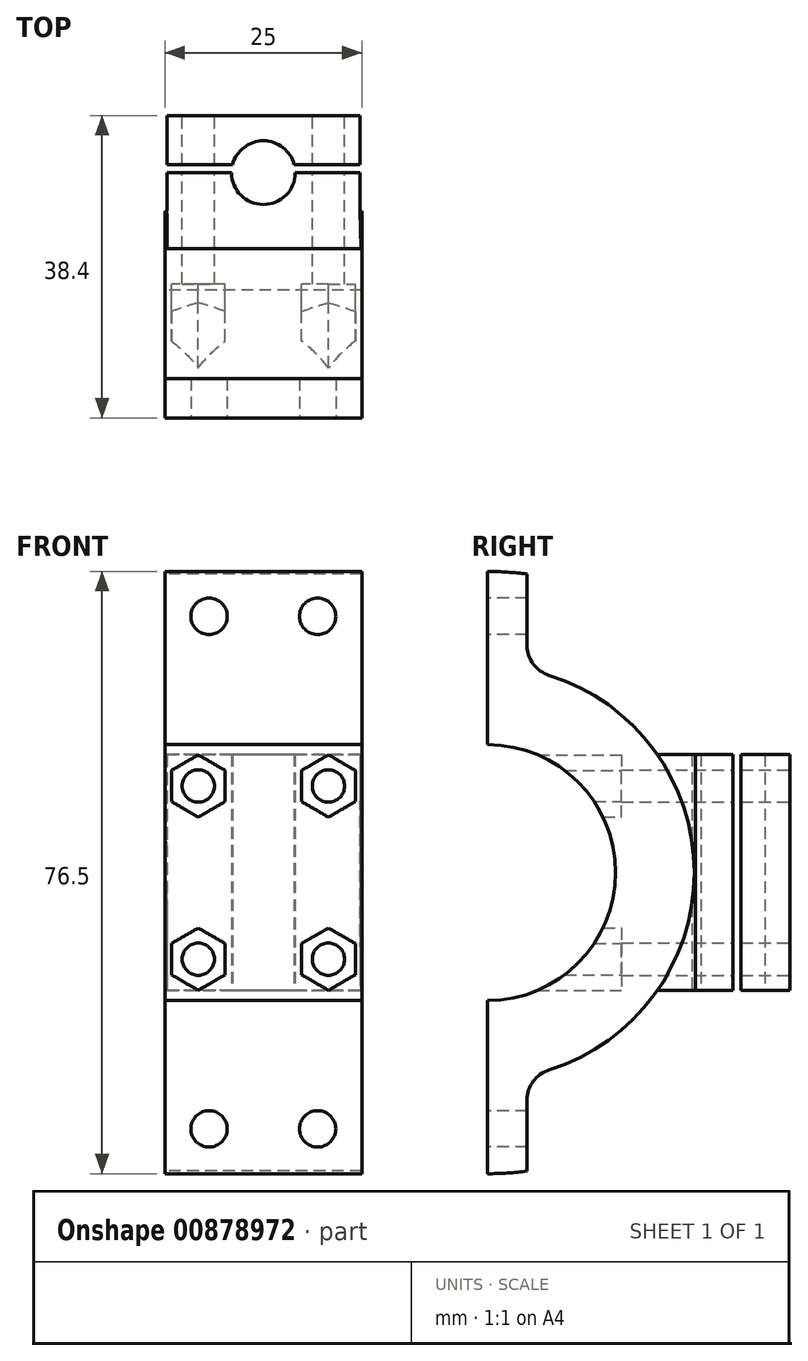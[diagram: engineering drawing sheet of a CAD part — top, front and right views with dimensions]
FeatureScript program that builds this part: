
annotation { "Feature Type Name" : "Feature", "Feature Type Description" : "" }
export const myFeature = defineFeature(function(context is Context, id is Id, definition is map)
    precondition{}
    {
        {
            var Q0;
            Q0=qCreatedBy(makeId("Right.planeOp"),FACE);
            var sketch = newSketch(context, id + "F0", { "sketchPlane" : qUnion([Q0])});
            skArc(sketch, "E0", {"start": v(0, -16.25) * mm, "mid": v(16.25, 0) * mm, "end": v(0, 16.25) * mm});
            skArc(sketch, "E1.0", {"start": v(7.8, -25.06) * mm, "mid": v(26.25, 0) * mm, "end": v(7.8, 25.06) * mm});
            skLineSegment(sketch, "E2", {"start": v(0, 16.25) * mm, "end": v(0, 38.25) * mm});
            skLineSegment(sketch, "E3", {"start": v(0, -16.25) * mm, "end": v(0, -38.25) * mm});
            skLineSegment(sketch, "E4.0", {"start": v(5, -28.88) * mm, "end": v(5, -37.92) * mm});
            skLineSegment(sketch, "E5.0", {"start": v(5, 28.88) * mm, "end": v(5, 37.92) * mm});
            skPoint(sketch, "E6.visualSharp", {"position": v(-5, 25.77) * mm});
            skPoint(sketch, "E7.visualSharp", {"position": v(5, 25.77) * mm});
            skArc(sketch, "E7.filletArc", {"start": v(5, 28.88) * mm, "mid": v(5.78, 26.5) * mm, "end": v(7.8, 25.06) * mm});
            skPoint(sketch, "E8.visualSharp", {"position": v(5, -25.77) * mm});
            skArc(sketch, "E8.filletArc", {"start": v(7.8, -25.06) * mm, "mid": v(5.78, -26.5) * mm, "end": v(5, -28.88) * mm});
            skPoint(sketch, "E9.visualSharp", {"position": v(-5, -25.77) * mm});
            skArc(sketch, "E10.0", {"start": v(5, 37.92) * mm, "mid": v(2.5, 38.17) * mm, "end": v(0, 38.25) * mm});
            skArc(sketch, "E11.MirrorCS", {"start": v(5, -37.92) * mm, "mid": v(2.5, -38.17) * mm, "end": v(0, -38.25) * mm});
            skSolve(sketch);
        }
        {
            var Q0;
            Q0=qSketchRegion(id+"F0",true);
            extrude(context, id + "F1", {"entities" : qUnion([Q0]), "endBound" : BoundingType.SYMMETRIC, "depth" : 25 * mm, "offsetDistance" : 25 * mm});
        }
        {
            var Q0;
            Q0=qCreatedBy(makeId("Front.planeOp"),FACE);
            var sketch = newSketch(context, id + "F2", { "sketchPlane" : qUnion([Q0])});
            skCircle(sketch, "E12", {"center": v(6.9, 32.56) * mm, "radius": 2.31 * mm});
            skCircle(sketch, "E13.MirrorC", {"center": v(-6.9, 32.56) * mm, "radius": 2.31 * mm});
            skCircle(sketch, "E14.MirrorC", {"center": v(-6.9, -32.56) * mm, "radius": 2.31 * mm});
            skCircle(sketch, "E15.MirrorC", {"center": v(6.9, -32.56) * mm, "radius": 2.31 * mm});
            skSolve(sketch);
        }
        {
            var Q0;
            Q0=qSketchRegion(id+"F2",true);
            extrude(context, id + "F3", {"entities" : qUnion([Q0]), "operationType" : NewBodyOperationType.REMOVE, "endBound" : BoundingType.THROUGH_ALL, "oppositeDirection" : true, "depth" : 25 * mm, "offsetDistance" : 25 * mm});
        }
        {
            var Q0;
            Q0=qCreatedBy(makeId("Top.planeOp"),FACE);
            var sketch = newSketch(context, id + "F4", { "sketchPlane" : qUnion([Q0])});
            skArc(sketch, "E16", {"start": v(-4.05, 31.16) * mm, "mid": v(0, 27.11) * mm, "end": v(4.05, 31.16) * mm});
            skArc(sketch, "E17", {"start": v(-12.27, 26.35) * mm, "mid": v(-12.27, 26.13) * mm, "end": v(-12.27, 25.92) * mm});
            skLineSegment(sketch, "E18", {"start": v(0, 38.4) * mm, "end": v(-12.27, 38.4) * mm});
            skLineSegment(sketch, "E19", {"start": v(-12.27, 26.35) * mm, "end": v(-12.27, 31.16) * mm});
            skLineSegment(sketch, "E20", {"start": v(10.13, 19.2) * mm, "end": v(-10.13, 19.2) * mm});
            skLineSegment(sketch, "E21", {"start": v(-4.05, 31.16) * mm, "end": v(-12.27, 31.16) * mm});
            skLineSegment(sketch, "E22.0", {"start": v(-3.92, 32.16) * mm, "end": v(-12.27, 32.16) * mm});
            skLineSegment(sketch, "E23.trimOffspring", {"start": v(-12.27, 32.16) * mm, "end": v(-12.27, 38.4) * mm});
            skLineSegment(sketch, "E24", {"start": v(12.26, 26.43) * mm, "end": v(12.44, 19.2) * mm});
            skLineSegment(sketch, "E25", {"start": v(-12.27, 26.35) * mm, "end": v(-12.27, 19.2) * mm});
            skLineSegment(sketch, "E26", {"start": v(-10.13, 19.2) * mm, "end": v(-12.27, 19.2) * mm});
            skLineSegment(sketch, "E27", {"start": v(10.13, 19.2) * mm, "end": v(12.44, 19.2) * mm});
            skLineSegment(sketch, "E28.MirrorCS", {"start": v(0, 38.4) * mm, "end": v(12.27, 38.4) * mm});
            skLineSegment(sketch, "E29.MirrorCS", {"start": v(12.27, 32.16) * mm, "end": v(12.27, 38.4) * mm});
            skLineSegment(sketch, "E30.MirrorCS", {"start": v(3.92, 32.16) * mm, "end": v(12.27, 32.16) * mm});
            skLineSegment(sketch, "E31.MirrorCS", {"start": v(4.05, 31.16) * mm, "end": v(12.27, 31.16) * mm});
            skLineSegment(sketch, "E32.MirrorCS", {"start": v(12.27, 26.35) * mm, "end": v(12.27, 31.16) * mm});
            skArc(sketch, "E33.trimOffspring", {"start": v(3.92, 32.16) * mm, "mid": v(0, 35.21) * mm, "end": v(-3.92, 32.16) * mm});
            skSolve(sketch);
        }
        {
            var Q0;
            Q0=qSketchRegion(id+"F4",true);
            extrude(context, id + "F5", {"entities" : qUnion([Q0]), "operationType" : NewBodyOperationType.ADD, "endBound" : BoundingType.SYMMETRIC, "depth" : 30 * mm, "offsetDistance" : 25 * mm});
        }
        {
            var Q0;
            Q0=makeQuery(id+"F5.opExtrude","SWEPT_FACE",FACE,{"disambiguationData":[OSD([sQuery(id+"F4.wireOp",EDGE,"E18"),sQuery(id+"F4.wireOp",EDGE,"E28.MirrorCS")])]});
            var sketch = newSketch(context, id + "F6", { "sketchPlane" : qUnion([Q0])});
            skCircle(sketch, "E34", {"center": v(-8.27, 11) * mm, "radius": 2.05 * mm});
            skCircle(sketch, "E35.MirrorC", {"center": v(8.27, 11) * mm, "radius": 2.05 * mm});
            skCircle(sketch, "E36.MirrorC", {"center": v(-8.27, -11) * mm, "radius": 2.05 * mm});
            skCircle(sketch, "E37.MirrorC", {"center": v(8.27, -11) * mm, "radius": 2.05 * mm});
            skPoint(sketch, "E38.0.end.orphan", {"position": v(-12.27, -15) * mm});
            skPoint(sketch, "E38.0.start.orphan", {"position": v(-12.27, 15) * mm});
            skSolve(sketch);
        }
        {
            var Q0;
            Q0=qSketchRegion(id+"F6",true);
            extrude(context, id + "F7", {"entities" : qUnion([Q0]), "operationType" : NewBodyOperationType.REMOVE, "oppositeDirection" : true, "depth" : 35 * mm, "offsetDistance" : 25 * mm});
        }
        {
            var Q0;
            Q0=qCreatedBy(makeId("Front.planeOp"),FACE);
            cPlane(context, id + "F8", {"entities" : qUnion([Q0]), "cplaneType" : CPlaneType.OFFSET, "offset" : 17 * mm, "oppositeDirection" : true, "width" : 150 * mm, "height" : 150 * mm});
        }
        {
            var Q0;
            Q0=qCreatedBy(id+"F8.planeOp",FACE);
            var sketch = newSketch(context, id + "F9", { "sketchPlane" : qUnion([Q0])});
            skCircle(sketch, "E39.0", {"center": v(8.27, 11) * mm, "radius": 2.05 * mm});
            skCircle(sketch, "E39.1", {"center": v(8.27, -11) * mm, "radius": 2.05 * mm});
            skCircle(sketch, "E40.0", {"center": v(-8.27, 11) * mm, "radius": 2.05 * mm});
            skCircle(sketch, "E41.0", {"center": v(-8.27, -11) * mm, "radius": 2.05 * mm});
            skCircle(sketch, "E42.cCircle", {"center": v(8.27, 11) * mm, "radius": 3.43 * mm, "construction": true});
            skLineSegment(sketch, "E42.0", {"start": v(4.84, 9.02) * mm, "end": v(4.84, 12.98) * mm});
            skLineSegment(sketch, "E42.1", {"start": v(4.84, 12.98) * mm, "end": v(8.27, 14.95) * mm});
            skLineSegment(sketch, "E42.2", {"start": v(8.27, 14.95) * mm, "end": v(11.7, 12.98) * mm});
            skLineSegment(sketch, "E42.3", {"start": v(11.7, 12.98) * mm, "end": v(11.7, 9.02) * mm});
            skLineSegment(sketch, "E42.4", {"start": v(11.7, 9.02) * mm, "end": v(8.27, 7.05) * mm});
            skLineSegment(sketch, "E42.5", {"start": v(8.27, 7.05) * mm, "end": v(4.84, 9.02) * mm});
            skPoint(sketch, "E42.0.midPoint", {"position": v(4.84, 11) * mm});
            skCircle(sketch, "E43.MirrorC", {"center": v(-8.27, 11) * mm, "radius": 3.43 * mm, "construction": true});
            skLineSegment(sketch, "E44.MirrorCS", {"start": v(-4.84, 12.98) * mm, "end": v(-8.27, 14.95) * mm});
            skLineSegment(sketch, "E45.MirrorCS", {"start": v(-8.27, 14.95) * mm, "end": v(-11.7, 12.98) * mm});
            skLineSegment(sketch, "E46.MirrorCS", {"start": v(-11.7, 12.98) * mm, "end": v(-11.7, 9.02) * mm});
            skLineSegment(sketch, "E47.MirrorCS", {"start": v(-11.7, 9.02) * mm, "end": v(-8.27, 7.05) * mm});
            skLineSegment(sketch, "E48.MirrorCS", {"start": v(-8.27, 7.05) * mm, "end": v(-4.84, 9.02) * mm});
            skLineSegment(sketch, "E49.MirrorCS", {"start": v(-4.84, 9.02) * mm, "end": v(-4.84, 12.98) * mm});
            skLineSegment(sketch, "E50.MirrorCS", {"start": v(4.84, -9.02) * mm, "end": v(4.84, -12.98) * mm});
            skLineSegment(sketch, "E51.MirrorCS", {"start": v(-11.7, -12.98) * mm, "end": v(-11.7, -9.02) * mm});
            skLineSegment(sketch, "E52.MirrorCS", {"start": v(8.27, -14.95) * mm, "end": v(11.7, -12.98) * mm});
            skLineSegment(sketch, "E53.MirrorCS", {"start": v(11.7, -9.02) * mm, "end": v(8.27, -7.05) * mm});
            skLineSegment(sketch, "E54.MirrorCS", {"start": v(4.84, -12.98) * mm, "end": v(8.27, -14.95) * mm});
            skLineSegment(sketch, "E55.MirrorCS", {"start": v(-11.7, -9.02) * mm, "end": v(-8.27, -7.05) * mm});
            skPoint(sketch, "E56.MirrorP", {"position": v(4.84, -11) * mm});
            skLineSegment(sketch, "E57.MirrorCS", {"start": v(-8.27, -7.05) * mm, "end": v(-4.84, -9.02) * mm});
            skLineSegment(sketch, "E58.MirrorCS", {"start": v(-4.84, -12.98) * mm, "end": v(-8.27, -14.95) * mm});
            skLineSegment(sketch, "E59.MirrorCS", {"start": v(-8.27, -14.95) * mm, "end": v(-11.7, -12.98) * mm});
            skCircle(sketch, "E60.MirrorC", {"center": v(8.27, -11) * mm, "radius": 3.43 * mm, "construction": true});
            skLineSegment(sketch, "E61.MirrorCS", {"start": v(8.27, -7.05) * mm, "end": v(4.84, -9.02) * mm});
            skLineSegment(sketch, "E62.MirrorCS", {"start": v(-4.84, -9.02) * mm, "end": v(-4.84, -12.98) * mm});
            skLineSegment(sketch, "E63.MirrorCS", {"start": v(11.7, -12.98) * mm, "end": v(11.7, -9.02) * mm});
            skCircle(sketch, "E64.MirrorC", {"center": v(-8.27, -11) * mm, "radius": 3.43 * mm, "construction": true});
            skSolve(sketch);
        }
        {
            var Q0;
            Q0=qSketchRegion(id+"F9",true);
            extrude(context, id + "F10", {"entities" : qUnion([Q0]), "operationType" : NewBodyOperationType.REMOVE, "depth" : 25 * mm, "offsetDistance" : 25 * mm});
        }
    });
